# Revit family: Loading-Dock-Equipment_Shelter_McGuire_TC300
name_source: partatom
category: Generic Models
units: mm (PartAtom-declared; Revit-internal decimal feet)

## family parameters
Always vertical = No
Can host rebar = No
Classification Number = 23.50.70.00
Cut with Voids When Loaded = No
Maintain Annotation Orientation = No
Part Type = Normal
Room Calculation Point = No
Round Connector Dimension = Use Diameter
Shared = No
Work Plane-Based = Yes

## types (1)
- Flexible Steel Frame
    Accent Material = Metal - Aluminum Trim
    Assembly Code = E1030300
    Default Elevation = 0' - 0"
    Description = McGuire Loading Dock Product as Specified
    Expected Lifespan (Years) = 0
    Frame Thickness = 0' - 1 3/8"
    Green Building-LEED = http://www.arcat.com
    Guide Color = Polyethylene Sheeting - Yellow
    Keynote = 11160
    Maintenance Schedule (Months) = 0
    Manufacturer = McGuire
    Manufacturer Fax = 262-255-4199
    Manufacturer Website = http://www.wbmcguire.com
    Material = Polyethylene Sheeting - Black
    Model = As Specified
    Panel Material = Metal - Steel
    Product Data = http://www.arcat.com
    Revision = R1_2017-01
    Sales Information = http://www.wbmcguire.com
    URL = http://www.wbmcguire.com
    Warranty Duration (Years) = 0

## geometry (parser evidence)
native form markers: Blend x14, Sweep x1
no freeform markers — native parametric forms only
